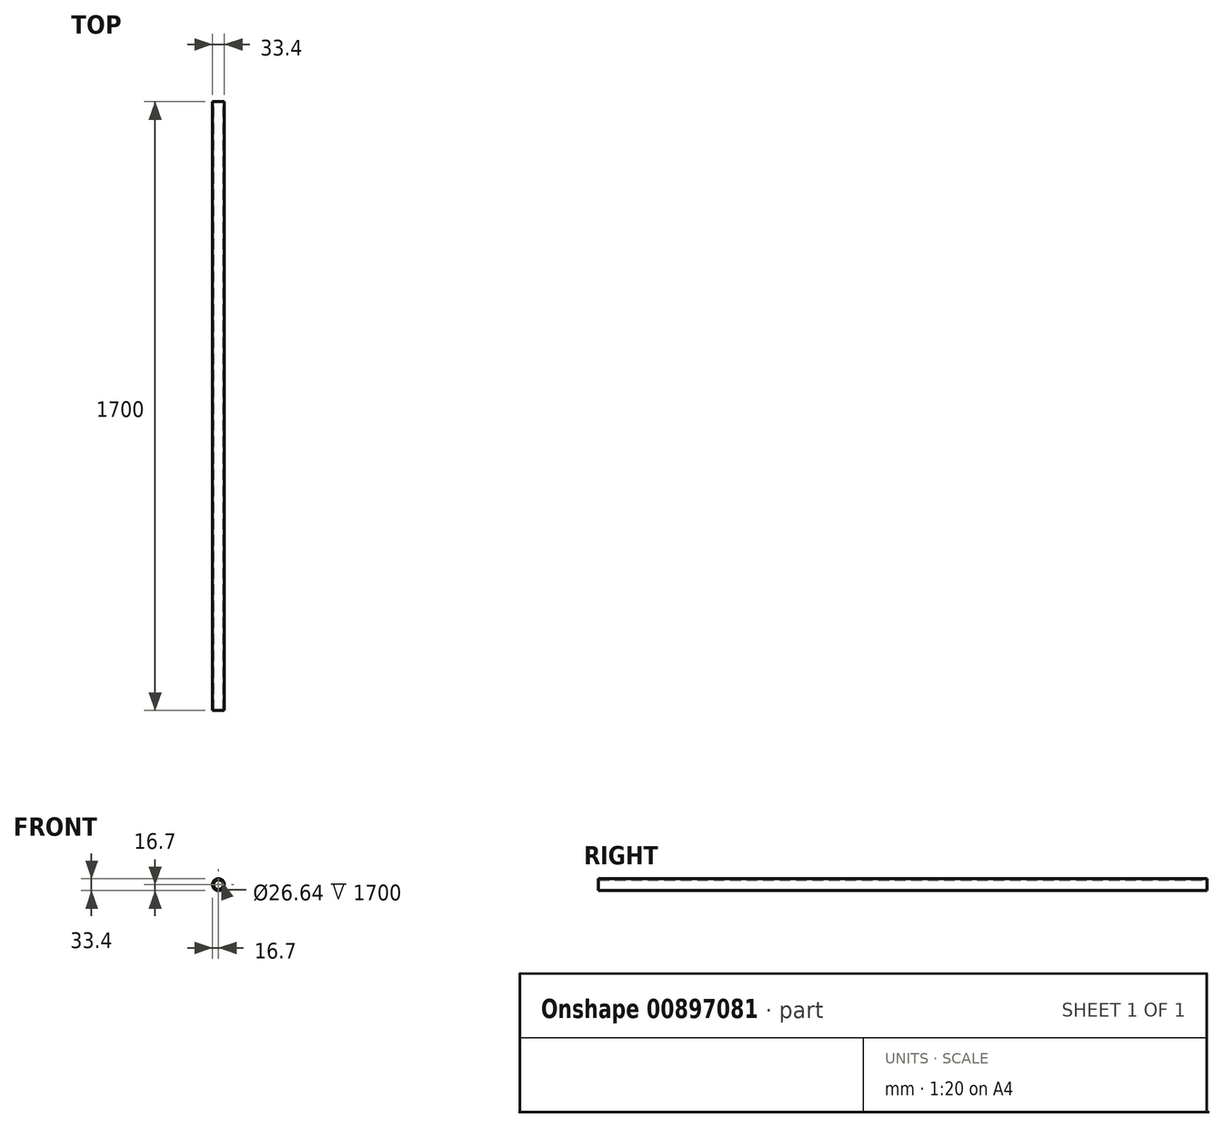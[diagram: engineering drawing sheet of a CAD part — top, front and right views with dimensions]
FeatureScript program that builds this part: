
annotation { "Feature Type Name" : "Feature", "Feature Type Description" : "" }
export const myFeature = defineFeature(function(context is Context, id is Id, definition is map)
    precondition{}
    {
        {
            var Q0;
            Q0=qCreatedBy(makeId("Front.planeOp"),FACE);
            var sketch = newSketch(context, id + "F0", { "sketchPlane" : qUnion([Q0])});
            skCircle(sketch, "E0", {"center": v(0, 0) * mm, "radius": 16.7 * mm});
            skCircle(sketch, "E1", {"center": v(0, 0) * mm, "radius": 13.32 * mm});
            skSolve(sketch);
        }
        {
            var Q0;
            Q0=makeQuery(id+"F0.imprint","IMPRINT",FACE,{"disambiguationData":[TD([[makeQuery(id+"F0.imprint","IMPRINT",EDGE,{"derivedFrom":sQuery(id+"F0.wireOp",EDGE,"E0")}),1.0]])]});
            extrude(context, id + "F1", {"entities" : qUnion([Q0]), "endBound" : BoundingType.SYMMETRIC, "depth" : 1700 * mm, "offsetDistance" : 25.4 * mm});
        }
    });
